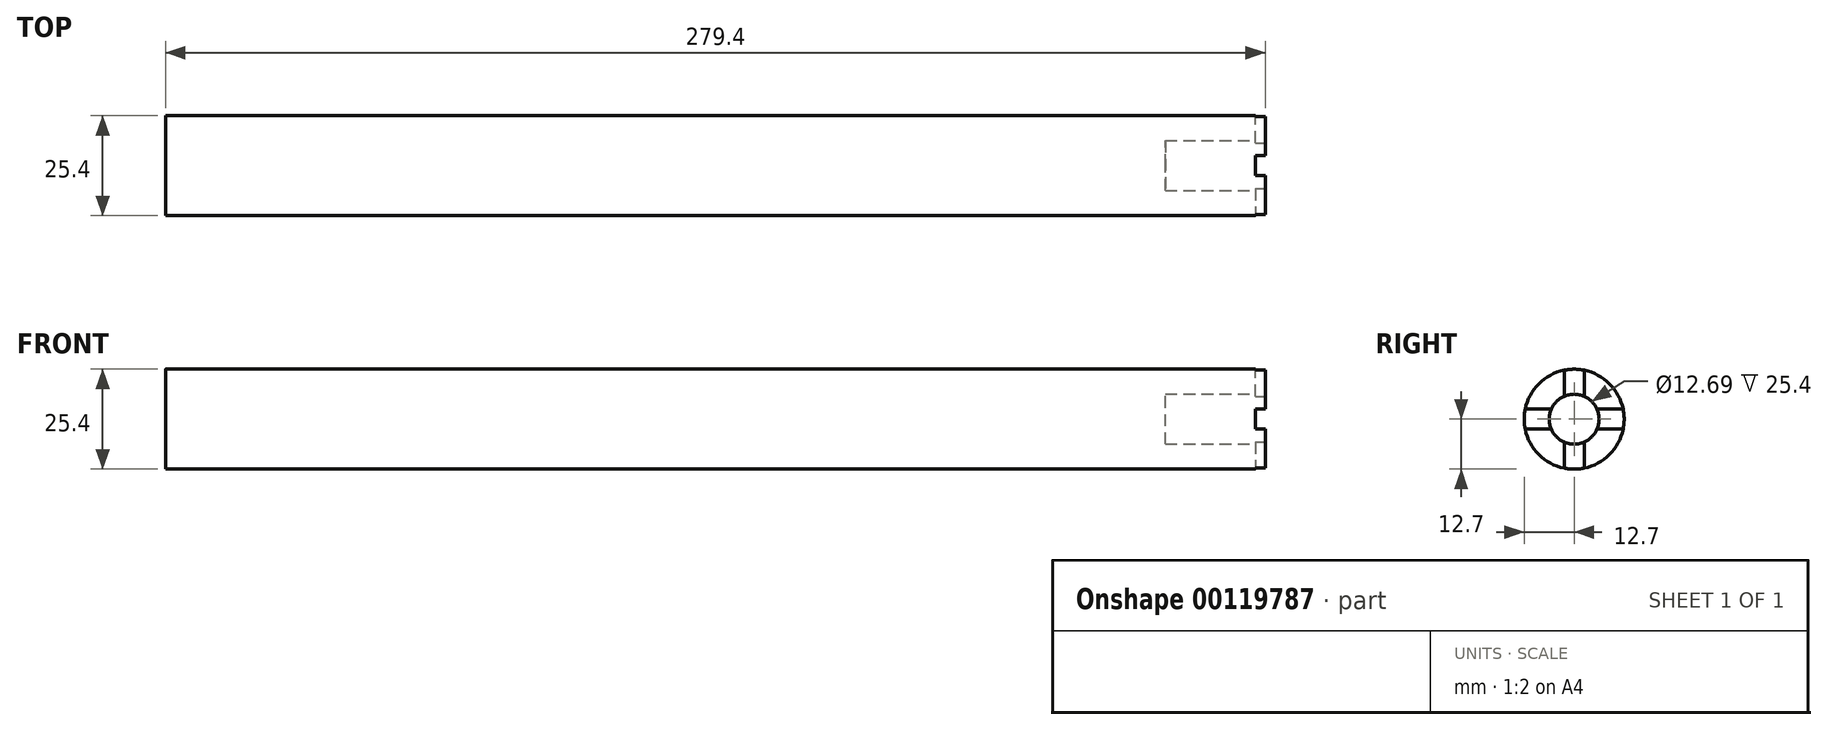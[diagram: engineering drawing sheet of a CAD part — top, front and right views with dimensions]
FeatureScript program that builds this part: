
annotation { "Feature Type Name" : "Feature", "Feature Type Description" : "" }
export const myFeature = defineFeature(function(context is Context, id is Id, definition is map)
    precondition{}
    {
        {
            var Q0;
            Q0=qCreatedBy(makeId("Right.planeOp"),FACE);
            var sketch = newSketch(context, id + "F0", { "sketchPlane" : qUnion([Q0])});
            skCircle(sketch, "E0", {"center": v(0, 0) * mm, "radius": 12.7 * mm});
            skSolve(sketch);
        }
        {
            var Q0;
            Q0 = qSketchRegion(id + "F0", true);
            extrude(context, id + "F1", {"entities" : qUnion([Q0]), "depth" : 279.4 * mm});
        }
        {
            var Q0;
            Q0=makeQuery(id+"F1.opExtrude","CAP_FACE",FACE,{"disambiguationData":[OSD([sQuery(id+"F0.wireOp",EDGE,"E0")])],"isStart":false});
            var sketch = newSketch(context, id + "F2", { "sketchPlane" : qUnion([Q0])});
            skLineSegment(sketch, "E1", {"start": v(0, 24.1) * mm, "end": v(0, -34.95) * mm, "construction": true});
            skLineSegment(sketch, "E2", {"start": v(-25.9, 0) * mm, "end": v(32.1, 0) * mm, "construction": true});
            skLineSegment(sketch, "E3.bottom", {"start": v(1.34, 2.54) * mm, "end": v(17.43, 2.54) * mm});
            skLineSegment(sketch, "E3.top", {"start": v(1.34, -2.54) * mm, "end": v(17.43, -2.54) * mm});
            skLineSegment(sketch, "E3.left", {"start": v(1.34, 2.54) * mm, "end": v(1.34, -2.54) * mm});
            skLineSegment(sketch, "E3.right", {"start": v(17.43, 2.54) * mm, "end": v(17.43, -2.54) * mm});
            skLineSegment(sketch, "E4.bottom", {"start": v(-2.54, 4.33) * mm, "end": v(2.54, 4.33) * mm});
            skLineSegment(sketch, "E4.top", {"start": v(-2.54, 18.02) * mm, "end": v(2.54, 18.02) * mm});
            skLineSegment(sketch, "E4.left", {"start": v(-2.54, 4.33) * mm, "end": v(-2.54, 18.02) * mm});
            skLineSegment(sketch, "E4.right", {"start": v(2.54, 4.33) * mm, "end": v(2.54, 18.02) * mm});
            skLineSegment(sketch, "E5.bottom", {"start": v(-2.62, 2.54) * mm, "end": v(-17.29, 2.54) * mm});
            skLineSegment(sketch, "E5.top", {"start": v(-2.62, -2.54) * mm, "end": v(-17.29, -2.54) * mm});
            skLineSegment(sketch, "E5.left", {"start": v(-2.62, 2.54) * mm, "end": v(-2.62, -2.54) * mm});
            skLineSegment(sketch, "E5.right", {"start": v(-17.29, 2.54) * mm, "end": v(-17.29, -2.54) * mm});
            skLineSegment(sketch, "E6.bottom", {"start": v(-2.54, -3.9) * mm, "end": v(2.54, -3.9) * mm});
            skLineSegment(sketch, "E6.top", {"start": v(-2.54, -17.4) * mm, "end": v(2.54, -17.4) * mm});
            skLineSegment(sketch, "E6.left", {"start": v(-2.54, -3.9) * mm, "end": v(-2.54, -17.4) * mm});
            skLineSegment(sketch, "E6.right", {"start": v(2.54, -3.9) * mm, "end": v(2.54, -17.4) * mm});
            skSolve(sketch);
        }
        {
            var Q0;
            {var subQ0=sQuery(id+"F2.wireOp",EDGE,"E3.right");Q0=makeQuery(id+"F2.imprint","IMPRINT",FACE,{"disambiguationData":[TD([[makeQuery(id+"F2.imprint","IMPRINT",EDGE,{"derivedFrom":subQ0}),-1.0]])]});}
            var Q1;
            {var subQ0=sQuery(id+"F2.wireOp",EDGE,"E4.top");Q1=makeQuery(id+"F2.imprint","IMPRINT",FACE,{"disambiguationData":[TD([[makeQuery(id+"F2.imprint","IMPRINT",EDGE,{"derivedFrom":subQ0}),-1.0]])]});}
            var Q2;
            {var subQ0=sQuery(id+"F2.wireOp",EDGE,"E5.right");Q2=makeQuery(id+"F2.imprint","IMPRINT",FACE,{"disambiguationData":[TD([[makeQuery(id+"F2.imprint","IMPRINT",EDGE,{"derivedFrom":subQ0}),1.0]])]});}
            var Q3;
            {var subQ0=sQuery(id+"F2.wireOp",EDGE,"E6.top");Q3=makeQuery(id+"F2.imprint","IMPRINT",FACE,{"disambiguationData":[TD([[makeQuery(id+"F2.imprint","IMPRINT",EDGE,{"derivedFrom":subQ0}),1.0]])]});}
            var Q4;
            {var subQ0=sQuery(id+"F2.wireOp",EDGE,"E3.left");Q4=makeQuery(id+"F2.imprint","IMPRINT",FACE,{"disambiguationData":[TD([[makeQuery(id+"F2.imprint","IMPRINT",EDGE,{"derivedFrom":subQ0}),1.0]])]});}
            var Q5;
            {var subQ0=sQuery(id+"F2.wireOp",EDGE,"E5.left");Q5=makeQuery(id+"F2.imprint","IMPRINT",FACE,{"disambiguationData":[TD([[makeQuery(id+"F2.imprint","IMPRINT",EDGE,{"derivedFrom":subQ0}),-1.0]])]});}
            var Q6;
            {var subQ0=sQuery(id+"F2.wireOp",EDGE,"E6.bottom");Q6=makeQuery(id+"F2.imprint","IMPRINT",FACE,{"disambiguationData":[TD([[makeQuery(id+"F2.imprint","IMPRINT",EDGE,{"derivedFrom":subQ0}),-1.0]])]});}
            var Q7;
            {var subQ0=sQuery(id+"F2.wireOp",EDGE,"E4.bottom");Q7=makeQuery(id+"F2.imprint","IMPRINT",FACE,{"disambiguationData":[TD([[makeQuery(id+"F2.imprint","IMPRINT",EDGE,{"derivedFrom":subQ0}),1.0]])]});}
            extrude(context, id + "F3", {"entities" : qUnion([Q0, Q1, Q2, Q3, Q4, Q5, Q6, Q7]), "operationType" : NewBodyOperationType.REMOVE, "oppositeDirection" : true, "depth" : 2.54 * mm});
        }
        {
            var Q0;
            Q0=makeQuery(id+"F1.opExtrude","CAP_FACE",FACE,{"disambiguationData":[OSD([sQuery(id+"F0.wireOp",EDGE,"E0")])],"isStart":false});
            var sketch = newSketch(context, id + "F4", { "sketchPlane" : qUnion([Q0])});
            skCircle(sketch, "E7", {"center": v(0, 0) * mm, "radius": 6.35 * mm});
            skSolve(sketch);
        }
        {
            var Q0;
            Q0 = qSketchRegion(id + "F4", true);
            extrude(context, id + "F5", {"entities" : qUnion([Q0]), "operationType" : NewBodyOperationType.REMOVE, "oppositeDirection" : true, "depth" : 25.4 * mm});
        }
    });
